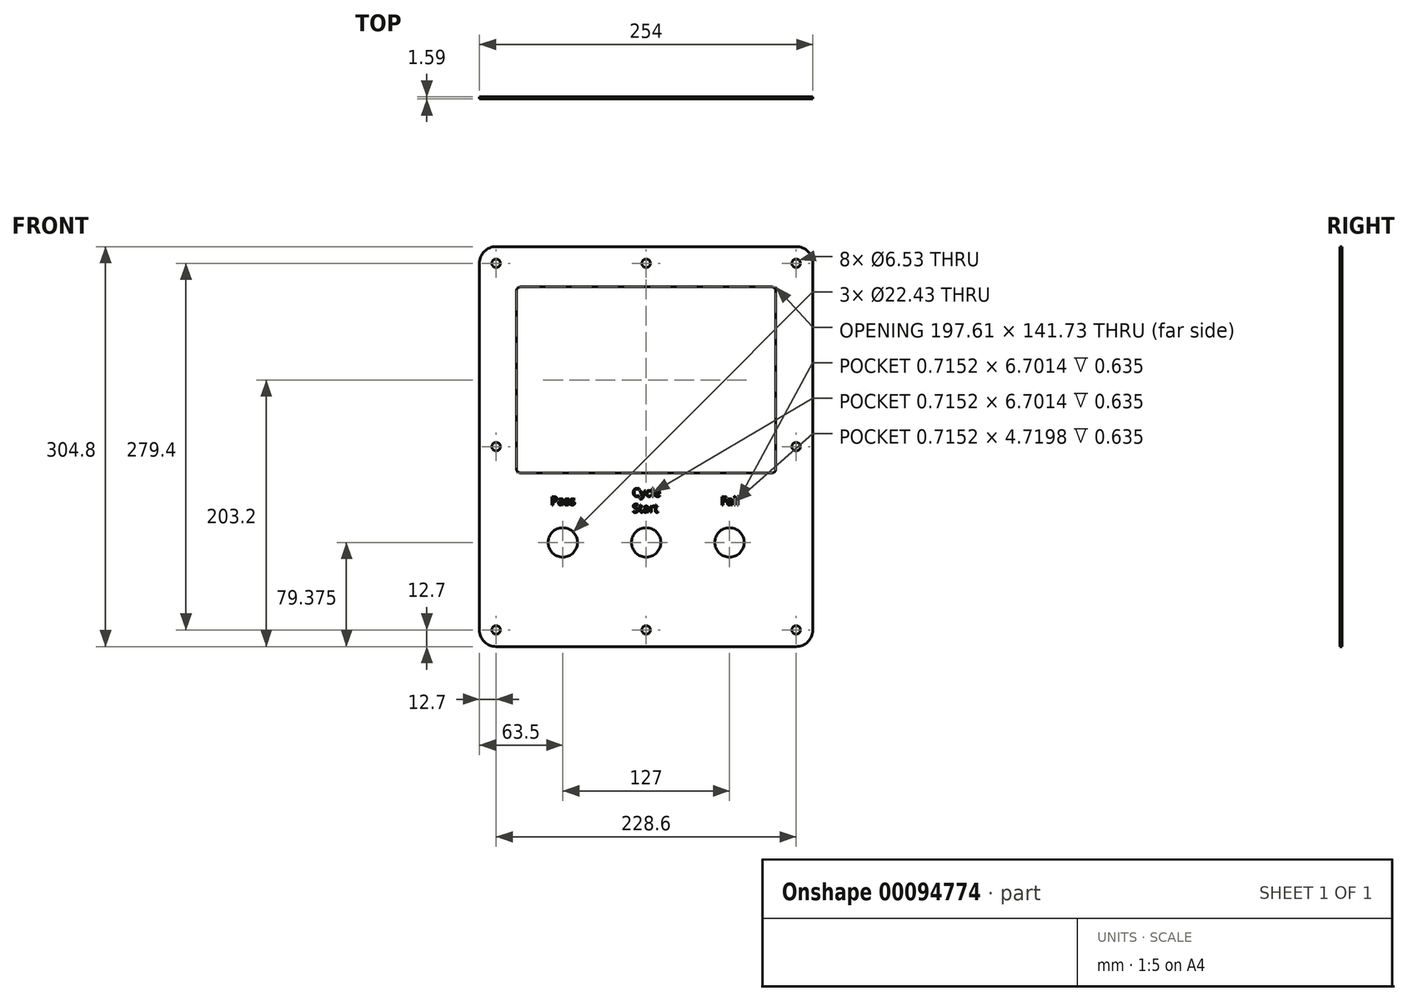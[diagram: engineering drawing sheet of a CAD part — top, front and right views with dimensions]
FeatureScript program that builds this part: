
annotation { "Feature Type Name" : "Feature", "Feature Type Description" : "" }
export const myFeature = defineFeature(function(context is Context, id is Id, definition is map)
    precondition{}
    {
        {
            var Q0;
            Q0=qCreatedBy(makeId("Front.planeOp"),FACE);
            var sketch = newSketch(context, id + "F0", { "sketchPlane" : qUnion([Q0])});
            skLineSegment(sketch, "E0.bottom", {"start": v(-114.3, 152.4) * mm, "end": v(114.3, 152.4) * mm});
            skLineSegment(sketch, "E0.top", {"start": v(-114.3, -152.4) * mm, "end": v(114.3, -152.4) * mm});
            skLineSegment(sketch, "E0.left", {"start": v(-127, 139.7) * mm, "end": v(-127, -139.7) * mm});
            skLineSegment(sketch, "E0.right", {"start": v(127, 139.7) * mm, "end": v(127, -139.7) * mm});
            skPoint(sketch, "E0.middle", {"position": v(0, 0) * mm});
            skPoint(sketch, "E1.visualSharp", {"position": v(-127, 152.4) * mm});
            skArc(sketch, "E1.filletArc", {"start": v(-114.3, 152.4) * mm, "mid": v(-123.28, 148.68) * mm, "end": v(-127, 139.7) * mm});
            skPoint(sketch, "E2.visualSharp", {"position": v(127, 152.4) * mm});
            skArc(sketch, "E2.filletArc", {"start": v(127, 139.7) * mm, "mid": v(123.28, 148.68) * mm, "end": v(114.3, 152.4) * mm});
            skPoint(sketch, "E3.visualSharp", {"position": v(127, -152.4) * mm});
            skArc(sketch, "E3.filletArc", {"start": v(114.3, -152.4) * mm, "mid": v(123.28, -148.68) * mm, "end": v(127, -139.7) * mm});
            skPoint(sketch, "E4.visualSharp", {"position": v(-127, -152.4) * mm});
            skArc(sketch, "E4.filletArc", {"start": v(-127, -139.7) * mm, "mid": v(-123.28, -148.68) * mm, "end": v(-114.3, -152.4) * mm});
            skSolve(sketch);
        }
        {
            var Q0;
            Q0 = qSketchRegion(id + "F0", true);
            extrude(context, id + "F1", {"entities" : qUnion([Q0]), "depth" : 1.59 * mm});
        }
        {
            var Q0;
            Q0=makeQuery(id+"F1.opExtrude","CAP_FACE",FACE,{"disambiguationData":[OSD([sQuery(id+"F0.wireOp",EDGE,"E0.bottom"),sQuery(id+"F0.wireOp",EDGE,"E0.top"),sQuery(id+"F0.wireOp",EDGE,"E0.left"),sQuery(id+"F0.wireOp",EDGE,"E0.right")])],"isStart":false});
            var sketch = newSketch(context, id + "F2", { "sketchPlane" : qUnion([Q0])});
            skCircle(sketch, "E5", {"center": v(-63.5, -73.03) * mm, "radius": 11.21 * mm});
            skCircle(sketch, "E6.1.0.0", {"center": v(0, -73.03) * mm, "radius": 11.21 * mm});
            skCircle(sketch, "E6.2.0.0", {"center": v(63.5, -73.02) * mm, "radius": 11.21 * mm});
            skLineSegment(sketch, "E6.direction1", {"start": v(-63.5, -73.02) * mm, "end": v(0, -73.02) * mm, "construction": true});
            skSolve(sketch);
        }
        {
            var Q0;
            Q0 = qSketchRegion(id + "F2", true);
            extrude(context, id + "F3", {"entities" : qUnion([Q0]), "operationType" : NewBodyOperationType.REMOVE, "oppositeDirection" : true, "depth" : 25.4 * mm});
        }
        {
            var Q0;
            Q0=makeQuery(id+"F1.opExtrude","CAP_FACE",FACE,{"disambiguationData":[OSD([sQuery(id+"F0.wireOp",EDGE,"E0.bottom"),sQuery(id+"F0.wireOp",EDGE,"E0.top"),sQuery(id+"F0.wireOp",EDGE,"E0.left"),sQuery(id+"F0.wireOp",EDGE,"E0.right")])],"isStart":false});
            var sketch = newSketch(context, id + "F4", { "sketchPlane" : qUnion([Q0])});
            skLineSegment(sketch, "E7.bottom", {"start": v(95.76, 121.67) * mm, "end": v(-95.76, 121.67) * mm});
            skLineSegment(sketch, "E7.top", {"start": v(95.76, -20.07) * mm, "end": v(-95.76, -20.07) * mm});
            skLineSegment(sketch, "E7.left", {"start": v(98.8, 118.62) * mm, "end": v(98.8, -17.02) * mm});
            skLineSegment(sketch, "E7.right", {"start": v(-98.8, 118.62) * mm, "end": v(-98.8, -17.02) * mm});
            skPoint(sketch, "E7.middle", {"position": v(0, 50.8) * mm});
            skPoint(sketch, "E8.visualSharp", {"position": v(-98.8, 121.67) * mm});
            skArc(sketch, "E8.filletArc", {"start": v(-95.76, 121.67) * mm, "mid": v(-97.91, 120.77) * mm, "end": v(-98.8, 118.62) * mm});
            skPoint(sketch, "E9.visualSharp", {"position": v(98.8, 121.67) * mm});
            skArc(sketch, "E9.filletArc", {"start": v(98.8, 118.62) * mm, "mid": v(97.91, 120.77) * mm, "end": v(95.76, 121.67) * mm});
            skPoint(sketch, "E10.visualSharp", {"position": v(98.8, -20.07) * mm});
            skArc(sketch, "E10.filletArc", {"start": v(95.76, -20.07) * mm, "mid": v(97.91, -19.17) * mm, "end": v(98.8, -17.02) * mm});
            skPoint(sketch, "E11.visualSharp", {"position": v(-98.8, -20.07) * mm});
            skArc(sketch, "E11.filletArc", {"start": v(-98.8, -17.02) * mm, "mid": v(-97.91, -19.17) * mm, "end": v(-95.76, -20.07) * mm});
            skSolve(sketch);
        }
        {
            var Q0;
            Q0 = qSketchRegion(id + "F4", true);
            extrude(context, id + "F5", {"entities" : qUnion([Q0]), "operationType" : NewBodyOperationType.REMOVE, "oppositeDirection" : true, "depth" : 25.4 * mm});
        }
        {
            var Q0;
            Q0=makeQuery(id+"F1.opExtrude","CAP_FACE",FACE,{"disambiguationData":[OSD([sQuery(id+"F0.wireOp",EDGE,"E0.bottom"),sQuery(id+"F0.wireOp",EDGE,"E0.top"),sQuery(id+"F0.wireOp",EDGE,"E0.left"),sQuery(id+"F0.wireOp",EDGE,"E0.right"),sQuery(id+"F0.wireOp",EDGE,"E1.filletArc"),sQuery(id+"F0.wireOp",EDGE,"E2.filletArc"),sQuery(id+"F0.wireOp",EDGE,"E3.filletArc"),sQuery(id+"F0.wireOp",EDGE,"E4.filletArc")])],"isStart":false});
            var sketch = newSketch(context, id + "F6", { "sketchPlane" : qUnion([Q0])});
            skCircle(sketch, "E12", {"center": v(-114.3, 139.7) * mm, "radius": 3.26 * mm});
            skCircle(sketch, "E13.0.1.0", {"center": v(-114.3, 0) * mm, "radius": 3.26 * mm});
            skCircle(sketch, "E13.0.2.0", {"center": v(-114.3, -139.7) * mm, "radius": 3.26 * mm});
            skCircle(sketch, "E13.1.0.0", {"center": v(0, 139.7) * mm, "radius": 3.26 * mm});
            skCircle(sketch, "E13.1.1.0", {"center": v(0, 0) * mm, "radius": 3.26 * mm});
            skCircle(sketch, "E13.1.2.0", {"center": v(0, -139.7) * mm, "radius": 3.26 * mm});
            skCircle(sketch, "E13.2.0.0", {"center": v(114.3, 139.7) * mm, "radius": 3.26 * mm});
            skCircle(sketch, "E13.2.1.0", {"center": v(114.3, 0) * mm, "radius": 3.26 * mm});
            skCircle(sketch, "E13.2.2.0", {"center": v(114.3, -139.7) * mm, "radius": 3.26 * mm});
            skLineSegment(sketch, "E13.direction1", {"start": v(-114.3, 139.7) * mm, "end": v(0, 139.7) * mm, "construction": true});
            skLineSegment(sketch, "E13.direction2", {"start": v(-114.3, 139.7) * mm, "end": v(-114.3, 0) * mm, "construction": true});
            skSolve(sketch);
        }
        {
            var Q0;
            Q0 = qSketchRegion(id + "F6", true);
            extrude(context, id + "F7", {"entities" : qUnion([Q0]), "operationType" : NewBodyOperationType.REMOVE, "oppositeDirection" : true, "depth" : 25.4 * mm});
        }
        {
            var Q0;
            Q0=makeQuery(id+"F1.opExtrude","CAP_FACE",FACE,{"disambiguationData":[OSD([sQuery(id+"F0.wireOp",EDGE,"E0.bottom"),sQuery(id+"F0.wireOp",EDGE,"E0.top"),sQuery(id+"F0.wireOp",EDGE,"E0.left"),sQuery(id+"F0.wireOp",EDGE,"E0.right"),sQuery(id+"F0.wireOp",EDGE,"E1.filletArc"),sQuery(id+"F0.wireOp",EDGE,"E2.filletArc"),sQuery(id+"F0.wireOp",EDGE,"E3.filletArc"),sQuery(id+"F0.wireOp",EDGE,"E4.filletArc")])],"isStart":false});
            var sketch = newSketch(context, id + "F8", { "sketchPlane" : qUnion([Q0])});
            skText(sketch, "E14", { "text": "Pass", "fontName": "OpenSans-Regular.ttf"});
            const initialGuessF8  = {"E14": [-0.07261, -0.04445, 1, 0, 0.00635]};
            skSetInitialGuess(sketch, initialGuessF8);
            skSolve(sketch);
        }
        {
            var Q0;
            {var subQ0=sQuery(id+"F0.wireOp",EDGE,"E0.left");var subQ1=sQuery(id+"F0.wireOp",EDGE,"E0.right");var subQ2=sQuery(id+"F0.wireOp",EDGE,"E0.top");var subQ3=sQuery(id+"F0.wireOp",EDGE,"E0.bottom");var subQ4=sQuery(id+"F0.wireOp",EDGE,"E1.filletArc");var subQ5=sQuery(id+"F0.wireOp",EDGE,"E2.filletArc");var subQ6=sQuery(id+"F0.wireOp",EDGE,"E3.filletArc");var subQ7=sQuery(id+"F0.wireOp",EDGE,"E4.filletArc");Q0=makeQuery(id+"F11.boolean.opBoolean","SPLIT",FACE,{"disambiguationData":[TD([makeQuery(id+"F1.opExtrude","SWEPT_FACE",FACE,{"disambiguationData":[OSD([subQ3])]})])],"derivedFrom":makeQuery(id+"F1.opExtrude","CAP_FACE",FACE,{"disambiguationData":[OSD([subQ3,subQ2,subQ0,subQ1,subQ4,subQ5,subQ6,subQ7])],"isStart":false})});}
            var sketch = newSketch(context, id + "F9", { "sketchPlane" : qUnion([Q0])});
            skText(sketch, "E15", { "text": "Cycle\nStart", "fontName": "OpenSans-Regular.ttf"});
            const initialGuessF9  = {"E15": [-0.0104, -0.0381, 1, 0, 0.00635]};
            skSetInitialGuess(sketch, initialGuessF9);
            skSolve(sketch);
        }
        {
            var Q0;
            {var subQ0=sQuery(id+"F0.wireOp",EDGE,"E0.top");var subQ1=sQuery(id+"F0.wireOp",EDGE,"E0.left");var subQ2=sQuery(id+"F0.wireOp",EDGE,"E0.bottom");var subQ3=sQuery(id+"F0.wireOp",EDGE,"E3.filletArc");var subQ4=sQuery(id+"F0.wireOp",EDGE,"E4.filletArc");var subQ5=sQuery(id+"F0.wireOp",EDGE,"E2.filletArc");var subQ6=sQuery(id+"F0.wireOp",EDGE,"E1.filletArc");var subQ7=sQuery(id+"F0.wireOp",EDGE,"E0.right");Q0=makeQuery(id+"F11.boolean.opBoolean","SPLIT",FACE,{"disambiguationData":[TD([makeQuery(id+"F1.opExtrude","SWEPT_FACE",FACE,{"disambiguationData":[OSD([subQ2])]})])],"derivedFrom":makeQuery(id+"F1.opExtrude","CAP_FACE",FACE,{"disambiguationData":[OSD([subQ2,subQ0,subQ1,subQ7,subQ6,subQ5,subQ3,subQ4])],"isStart":false})});}
            var sketch = newSketch(context, id + "F10", { "sketchPlane" : qUnion([Q0])});
            skText(sketch, "E16", { "text": "Fail", "fontName": "OpenSans-Regular.ttf"});
            const initialGuessF10  = {"E16": [0.05692, -0.04445, 1, 0, 0.00635]};
            skSetInitialGuess(sketch, initialGuessF10);
            skSolve(sketch);
        }
        {
            var Q0;
            Q0 = qSketchRegion(id + "F8", true);
            var Q1;
            Q1 = qSketchRegion(id + "F9", true);
            var Q2;
            Q2 = qSketchRegion(id + "F10", true);
            extrude(context, id + "F11", {"entities" : qUnion([Q0, Q1, Q2]), "operationType" : NewBodyOperationType.REMOVE, "oppositeDirection" : true, "depth" : 0.64 * mm});
        }
    });
